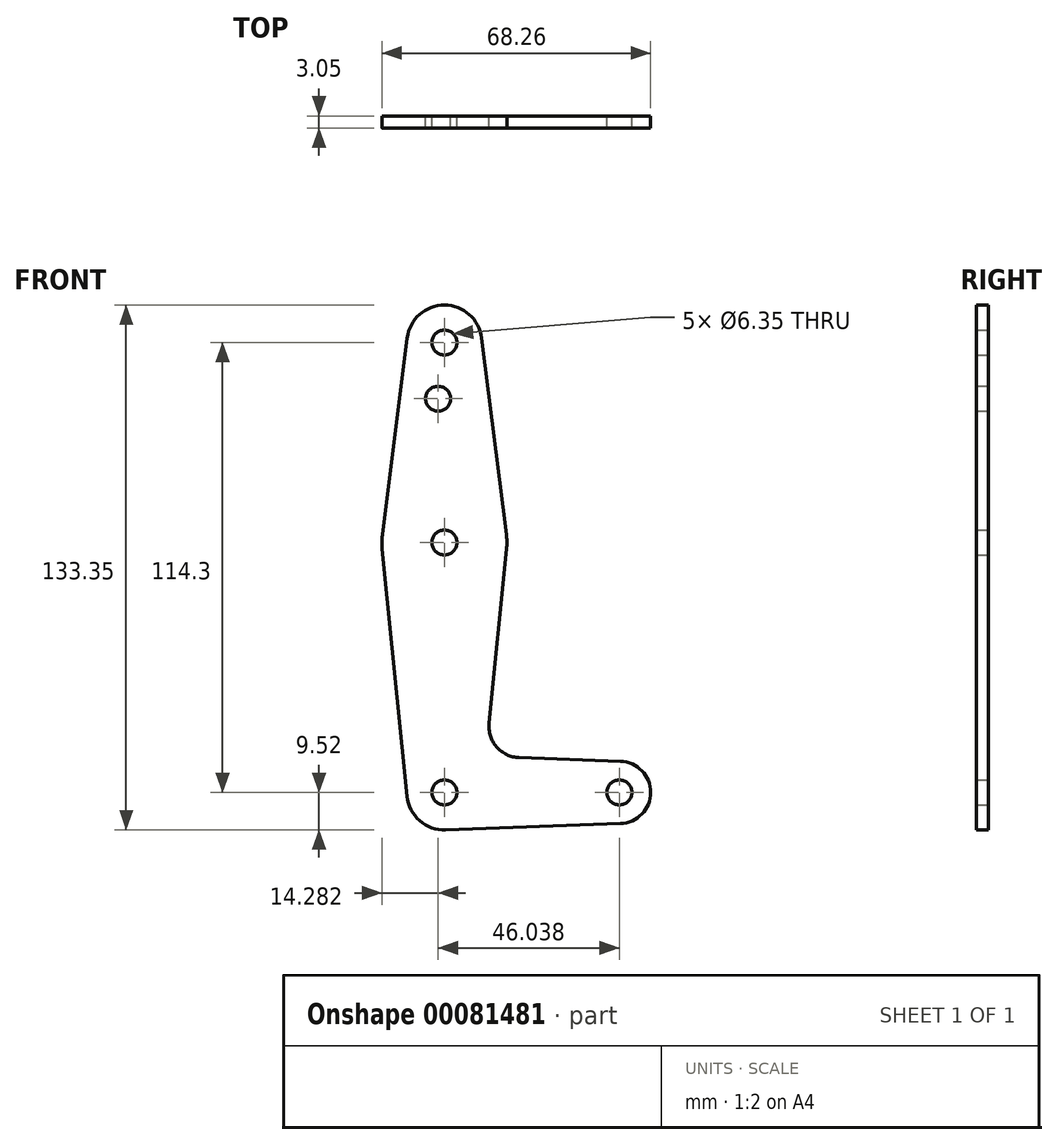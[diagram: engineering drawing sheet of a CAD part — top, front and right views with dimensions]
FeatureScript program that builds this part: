
annotation { "Feature Type Name" : "Feature", "Feature Type Description" : "" }
export const myFeature = defineFeature(function(context is Context, id is Id, definition is map)
    precondition{}
    {
        {
            var Q0;
            Q0=qCreatedBy(makeId("Front.planeOp"),FACE);
            var sketch = newSketch(context, id + "F0", { "sketchPlane" : qUnion([Q0])});
            skCircle(sketch, "E0", {"center": v(0, 0) * mm, "radius": 9.53 * mm});
            skCircle(sketch, "E1", {"center": v(0, 63.5) * mm, "radius": 15.88 * mm});
            skCircle(sketch, "E2", {"center": v(0, 114.3) * mm, "radius": 9.53 * mm});
            skCircle(sketch, "E3", {"center": v(44.45, 0) * mm, "radius": 7.94 * mm});
            skLineSegment(sketch, "E4", {"start": v(-9.45, 115.5) * mm, "end": v(-15.75, 65.48) * mm});
            skLineSegment(sketch, "E5", {"start": v(9.45, 115.5) * mm, "end": v(15.75, 65.48) * mm});
            skLineSegment(sketch, "E6", {"start": v(-15.8, 61.91) * mm, "end": v(-9.48, -0.95) * mm});
            skLineSegment(sketch, "E7", {"start": v(15.8, 61.91) * mm, "end": v(11.34, 17.6) * mm});
            skLineSegment(sketch, "E8", {"start": v(0.34, -9.52) * mm, "end": v(44.73, -7.93) * mm});
            skLineSegment(sketch, "E9", {"start": v(18.97, 8.85) * mm, "end": v(44.73, 7.93) * mm});
            skArc(sketch, "E10.filletArc", {"start": v(11.34, 17.6) * mm, "mid": v(13.26, 11.57) * mm, "end": v(18.97, 8.85) * mm});
            skLineSegment(sketch, "E11", {"start": v(0, 114.3) * mm, "end": v(0, 0) * mm, "construction": true});
            skLineSegment(sketch, "E12", {"start": v(44.45, 0) * mm, "end": v(0, 0) * mm, "construction": true});
            skCircle(sketch, "E13", {"center": v(0, 63.5) * mm, "radius": 3.18 * mm});
            skCircle(sketch, "E14", {"center": v(0, 0) * mm, "radius": 3.18 * mm});
            skCircle(sketch, "E15", {"center": v(44.45, 0) * mm, "radius": 3.18 * mm});
            skCircle(sketch, "E16", {"center": v(-1.59, 100.03) * mm, "radius": 3.18 * mm});
            skCircle(sketch, "E17", {"center": v(0, 114.3) * mm, "radius": 3.18 * mm});
            skSolve(sketch);
        }
        {
            var Q0;
            Q0 = qSketchRegion(id + "F0", true);
            extrude(context, id + "F1", {"entities" : qUnion([Q0]), "depth" : 3.05 * mm});
        }
    });
